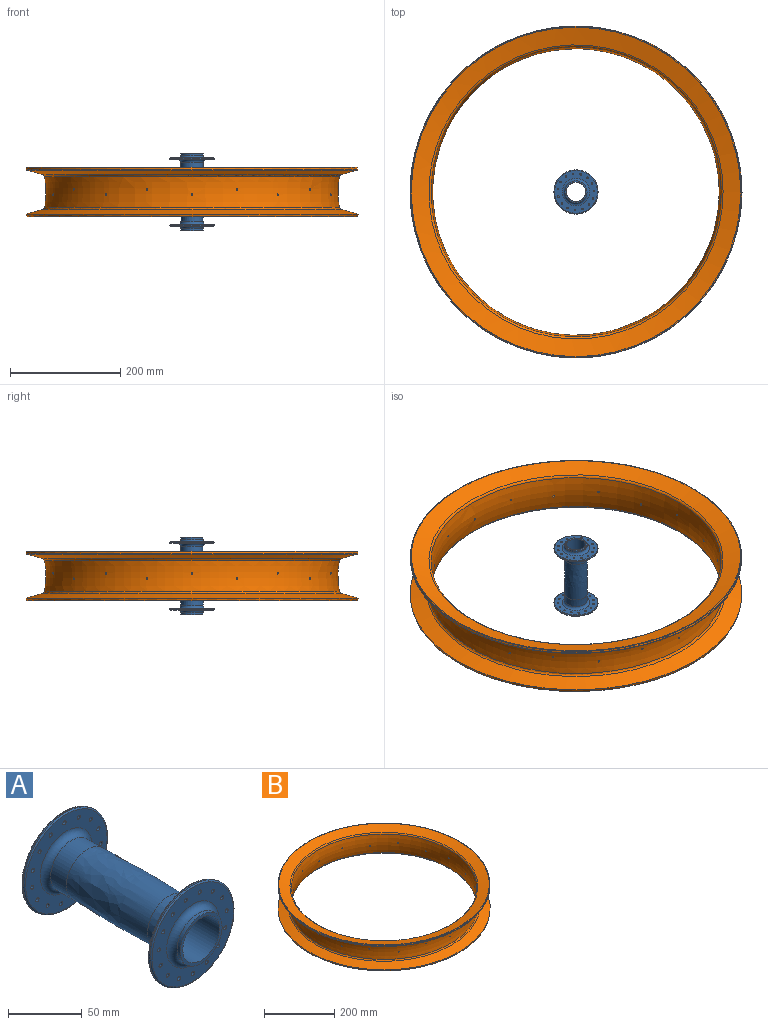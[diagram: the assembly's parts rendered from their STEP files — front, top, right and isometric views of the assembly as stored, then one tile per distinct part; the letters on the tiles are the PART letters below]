
ASSEMBLY  parts=2 mates=1
PART A: 52 faces, bbox 86.6x140.6x86.6 mm
  f0: cylinder r=20mm len=40mm, axis (0,-1,0), area 377mm2, adj f1,f16
  f1: torus R=25mm, axis (0,-1,0), area 1076.6mm2, adj f0,f2
  f2: plane 78x78mm, normal (0,1,0), area 2708.8mm2, adj f1,f17,f37,f38,f39,f40,f41,f42
  f3: cylinder r=40mm len=80mm, axis (0,-1,0), area 251.3mm2, adj f17,f18
  f4: plane 78x78mm, normal (0,-1,0), area 2708.8mm2, adj f5,f18,f37,f38,f39,f40,f41,f42
  f5: torus R=25mm, axis (0,-1,0), area 1076.6mm2, adj f4,f6
  f6: cylinder r=20mm len=40mm, axis (0,-1,0), area 1885mm2, adj f5,f7
  f7: revolved ~78x41.76mm, area 10111.9mm2, adj f6,f8
  f8: cone r=20mm half-angle=1deg, axis (0,1,0), area 1898mm2, adj f7,f9
  f9: torus R=25mm, axis (0,-1,0), area 1076.6mm2, adj f8,f10
  f10: plane 78x78mm, normal (0,1,0), area 2708.8mm2, adj f9,f19,f22,f23,f24,f25,f26,f27
  f11: cylinder r=40mm len=80mm, axis (0,-1,0), area 251.3mm2, adj f19,f20
  f12: plane 78x78mm, normal (0,-1,0), area 2708.8mm2, adj f13,f20,f22,f23,f24,f25,f26,f27
  f13: torus R=25mm, axis (0,-1,0), area 1076.6mm2, adj f12,f14
  f14: cylinder r=20mm len=40mm, axis (0,-1,0), area 377mm2, adj f13,f15
  f15: plane 40x40mm, normal (0,-1,0), area 289.9mm2, adj f14,f21
  f16: plane 40x40mm, normal (0,1,0), area 289.9mm2, adj f0,f21
  f17: torus R=39mm, axis (0,1,0), area 391.2mm2, adj f2,f3
  f18: torus R=39mm, axis (0,-1,0), area 391.2mm2, adj f3,f4
  f19: torus R=39mm, axis (0,1,0), area 391.2mm2, adj f10,f11
  f20: torus R=39mm, axis (0,-1,0), area 391.2mm2, adj f11,f12
  f21: cylinder r=17.54mm len=140mm, axis (0,-1,0), area 15431.1mm2, adj f15,f16
  f22: cylinder r=1.5mm len=3mm, axis (0,-1,0), area 28.3mm2, adj f10,f12
  f23: cylinder r=1.5mm len=3mm, axis (0,-1,0), area 28.3mm2, adj f10,f12
  f24: cylinder r=1.5mm len=3mm, axis (0,-1,0), area 28.3mm2, adj f10,f12
  f25: cylinder r=1.5mm len=3mm, axis (0,-1,0), area 28.3mm2, adj f10,f12
  f26: cylinder r=1.5mm len=3mm, axis (0,-1,0), area 28.3mm2, adj f10,f12
  f27: cylinder r=1.5mm len=3mm, axis (0,-1,0), area 28.3mm2, adj f10,f12
  f28: cylinder r=1.5mm len=3mm, axis (0,-1,0), area 28.3mm2, adj f10,f12
  f29: cylinder r=1.5mm len=3mm, axis (0,-1,0), area 28.3mm2, adj f10,f12
  f30: cylinder r=1.5mm len=3mm, axis (0,-1,0), area 28.3mm2, adj f10,f12
  f31: cylinder r=1.5mm len=3mm, axis (0,-1,0), area 28.3mm2, adj f10,f12
  f32: cylinder r=1.5mm len=3mm, axis (0,-1,0), area 28.3mm2, adj f10,f12
  f33: cylinder r=1.5mm len=3mm, axis (0,-1,0), area 28.3mm2, adj f10,f12
  f34: cylinder r=1.5mm len=3mm, axis (0,-1,0), area 28.3mm2, adj f10,f12
  f35: cylinder r=1.5mm len=3mm, axis (0,-1,0), area 28.3mm2, adj f10,f12
  f36: cylinder r=1.5mm len=3mm, axis (0,-1,0), area 28.3mm2, adj f10,f12
  f37: cylinder r=1.5mm len=3mm, axis (0,1,0), area 28.3mm2, adj f2,f4
  f38: cylinder r=1.5mm len=3mm, axis (0,1,0), area 28.3mm2, adj f2,f4
  f39: cylinder r=1.5mm len=3mm, axis (0,1,0), area 28.3mm2, adj f2,f4
  f40: cylinder r=1.5mm len=3mm, axis (0,1,0), area 28.3mm2, adj f2,f4
  f41: cylinder r=1.5mm len=3mm, axis (0,1,0), area 28.3mm2, adj f2,f4
  f42: cylinder r=1.5mm len=3mm, axis (0,1,0), area 28.3mm2, adj f2,f4
  f43: cylinder r=1.5mm len=3mm, axis (0,1,0), area 28.3mm2, adj f2,f4
  f44: cylinder r=1.5mm len=3mm, axis (0,1,0), area 28.3mm2, adj f2,f4
  f45: cylinder r=1.5mm len=3mm, axis (0,1,0), area 28.3mm2, adj f2,f4
  f46: cylinder r=1.5mm len=3mm, axis (0,1,0), area 28.3mm2, adj f2,f4
  f47: cylinder r=1.5mm len=3mm, axis (0,1,0), area 28.3mm2, adj f2,f4
  f48: cylinder r=1.5mm len=3mm, axis (0,1,0), area 28.3mm2, adj f2,f4
  f49: cylinder r=1.5mm len=3mm, axis (0,1,0), area 28.3mm2, adj f2,f4
  f50: cylinder r=1.5mm len=3mm, axis (0,1,0), area 28.3mm2, adj f2,f4
  f51: cylinder r=1.5mm len=3mm, axis (0,1,0), area 28.3mm2, adj f2,f4
PART B: 34 faces, bbox 664.7x664.7x213 mm
  f0: cone r=300mm half-angle=15.6deg, axis (0,0,-1), area 5667.5mm2, adj f12,f13
  f1: cone r=300mm half-angle=15.6deg, axis (0,0,1), area 9445.9mm2, adj f2,f5
  f2: cone r=268.35mm half-angle=74.4deg, axis (0,0,-1), area 56141.7mm2, adj f1,f10
  f3: torus R=410mm, axis (0,0,1), area 93840.7mm2, adj f10,f11,f14,f15,f16,f17,f18,f19
  f4: cone r=301.34mm half-angle=74.4deg, axis (0,0,1), area 54251.3mm2, adj f11,f13
  f5: cone r=267.01mm half-angle=74.4deg, axis (0,0,-1), area 61015.3mm2, adj f1,f6
  f6: torus R=268.35mm, axis (0,0,1), area 9016.7mm2, adj f5,f7
  f7: torus R=410mm, axis (0,0,1), area 105866mm2, adj f6,f8,f14,f15,f16,f17,f18,f19
  f8: torus R=268.35mm, axis (0,0,1), area 9016.7mm2, adj f7,f9
  f9: cone r=300mm half-angle=74.4deg, axis (0,0,1), area 59133.3mm2, adj f8,f12
  f10: torus R=272.63mm, axis (0,0,1), area 9342mm2, adj f2,f3
  f11: torus R=272.63mm, axis (0,0,1), area 9342mm2, adj f3,f4
  f12: torus R=299.31mm, axis (0,0,-1), area 2958.4mm2, adj f0,f9
  f13: torus R=300.11mm, axis (0,0,-1), area 2969.7mm2, adj f0,f4
  f14: cylinder r=1.5mm len=5.11mm, axis (1,0,0), area 47.2mm2, adj f3,f7
  f15: cylinder r=1.5mm len=5.89mm, axis (0.81,0.59,0), area 47.2mm2, adj f3,f7
  f16: cylinder r=1.5mm len=5.78mm, axis (0.31,0.95,0), area 47.2mm2, adj f3,f7
  f17: cylinder r=1.5mm len=5.78mm, axis (-0.31,0.95,0), area 47.2mm2, adj f3,f7
  f18: cylinder r=1.5mm len=5.89mm, axis (-0.81,0.59,0), area 47.2mm2, adj f3,f7
  f19: cylinder r=1.5mm len=5.11mm, axis (-1,0,0), area 47.2mm2, adj f3,f7
  f20: cylinder r=1.5mm len=5.89mm, axis (-0.81,-0.59,0), area 47.2mm2, adj f3,f7
  f21: cylinder r=1.5mm len=5.78mm, axis (-0.31,-0.95,0), area 47.2mm2, adj f3,f7
  f22: cylinder r=1.5mm len=5.78mm, axis (0.31,-0.95,0), area 47.2mm2, adj f3,f7
  f23: cylinder r=1.5mm len=5.89mm, axis (0.81,-0.59,0), area 47.2mm2, adj f3,f7
  f24: cylinder r=1.5mm len=5.11mm, axis (0,-1,0), area 47.2mm2, adj f3,f7
  f25: cylinder r=1.5mm len=5.89mm, axis (0.59,-0.81,0), area 47.2mm2, adj f3,f7
  f26: cylinder r=1.5mm len=5.78mm, axis (0.95,-0.31,0), area 47.2mm2, adj f3,f7
  f27: cylinder r=1.5mm len=5.78mm, axis (0.95,0.31,0), area 47.2mm2, adj f3,f7
  f28: cylinder r=1.5mm len=5.89mm, axis (0.59,0.81,0), area 47.2mm2, adj f3,f7
  f29: cylinder r=1.5mm len=5.11mm, axis (0,1,0), area 47.2mm2, adj f3,f7
  f30: cylinder r=1.5mm len=5.89mm, axis (-0.59,0.81,0), area 47.2mm2, adj f3,f7
  f31: cylinder r=1.5mm len=5.78mm, axis (-0.95,0.31,0), area 47.2mm2, adj f3,f7
  f32: cylinder r=1.5mm len=5.78mm, axis (-0.95,-0.31,0), area 47.2mm2, adj f3,f7
  f33: cylinder r=1.5mm len=5.89mm, axis (-0.59,-0.81,0), area 47.2mm2, adj f3,f7
PLACE A rot(axis=(1,0,0),90deg) t=(-138.95,-2.34,160.88)mm
PLACE B t=(-138.95,-2.34,160.88)mm
MATE fastened A.f0 <-> B.f0  axis (0,0,-1) through (-138.95,-2.34,160.88)mm
